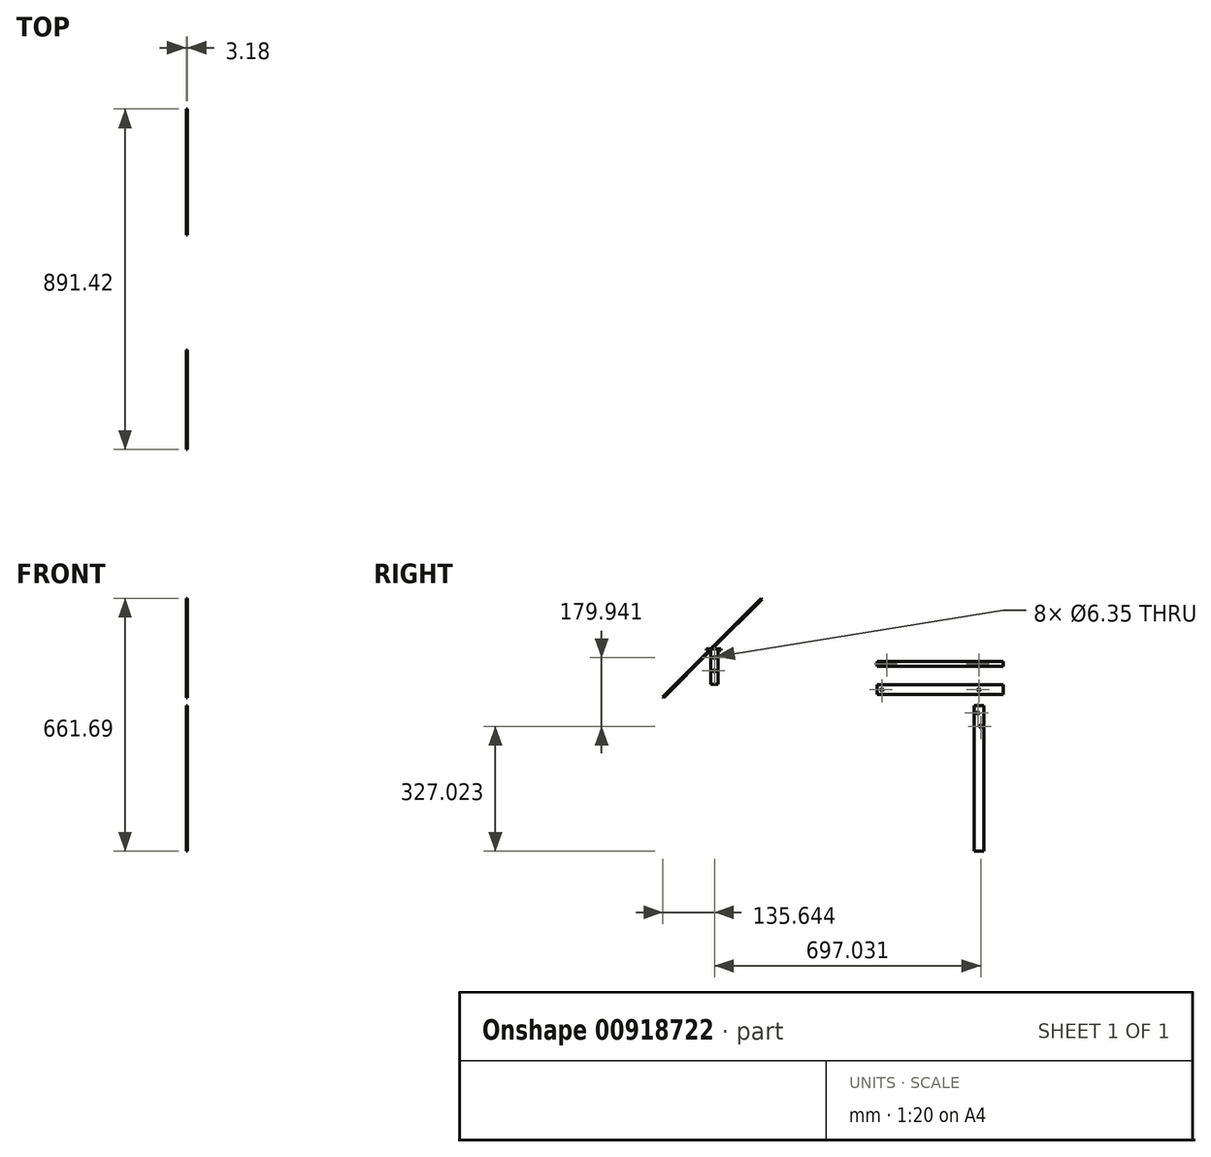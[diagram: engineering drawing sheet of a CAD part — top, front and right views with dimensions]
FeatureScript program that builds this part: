
annotation { "Feature Type Name" : "Feature", "Feature Type Description" : "" }
export const myFeature = defineFeature(function(context is Context, id is Id, definition is map)
    precondition{}
    {
        {
            var Q0;
            Q0=qCreatedBy(makeId("Right.planeOp"),FACE);
            var sketch = newSketch(context, id + "F0", { "sketchPlane" : qUnion([Q0])});
            skLineSegment(sketch, "E0.bottom", {"start": v(29.61, 247) * mm, "end": v(55.01, 247) * mm});
            skLineSegment(sketch, "E0.top", {"start": v(29.61, -134) * mm, "end": v(55.01, -134) * mm});
            skLineSegment(sketch, "E0.left", {"start": v(29.61, 247) * mm, "end": v(29.61, -134) * mm});
            skLineSegment(sketch, "E0.right", {"start": v(55.01, 247) * mm, "end": v(55.01, -134) * mm});
            skCircle(sketch, "E1", {"center": v(39.14, 227.96) * mm, "radius": 3.18 * mm});
            skCircle(sketch, "E2", {"center": v(46.76, 193.03) * mm, "radius": 3.18 * mm});
            skSolve(sketch);
        }
        {
            var Q0;
            Q0 = qSketchRegion(id + "F0", true);
            extrude(context, id + "F1", {"entities" : qUnion([Q0]), "depth" : 3.17 * mm, "offsetDistance" : 25.4 * mm});
        }
        {
            var Q0;
            Q0=qCreatedBy(makeId("Right.planeOp"),FACE);
            var sketch = newSketch(context, id + "F2", { "sketchPlane" : qUnion([Q0])});
            skLineSegment(sketch, "E3.bottom", {"start": v(-224.7, 301.37) * mm, "end": v(105.5, 301.37) * mm});
            skLineSegment(sketch, "E3.top", {"start": v(-224.7, 275.97) * mm, "end": v(105.5, 275.97) * mm});
            skLineSegment(sketch, "E3.left", {"start": v(-224.7, 301.37) * mm, "end": v(-224.7, 275.97) * mm});
            skLineSegment(sketch, "E3.right", {"start": v(105.5, 301.37) * mm, "end": v(105.5, 275.97) * mm});
            skLineSegment(sketch, "E4", {"start": v(105.5, 288.67) * mm, "end": v(-224.7, 288.67) * mm, "construction": true});
            skCircle(sketch, "E5", {"center": v(42, 288.67) * mm, "radius": 3.18 * mm});
            skCircle(sketch, "E6", {"center": v(-212, 288.67) * mm, "radius": 3.18 * mm});
            skLineSegment(sketch, "E7.bottom", {"start": v(105.5, 363.24) * mm, "end": v(-224.7, 363.24) * mm});
            skLineSegment(sketch, "E7.top", {"start": v(105.5, 350.54) * mm, "end": v(-224.7, 350.54) * mm});
            skLineSegment(sketch, "E7.left", {"start": v(105.5, 363.24) * mm, "end": v(105.5, 350.54) * mm});
            skLineSegment(sketch, "E7.right", {"start": v(-224.7, 363.24) * mm, "end": v(-224.7, 350.54) * mm});
            skLineSegment(sketch, "E8", {"start": v(-224.7, 356.9) * mm, "end": v(105.5, 356.9) * mm, "construction": true});
            skCircle(sketch, "E9", {"center": v(42, 356.9) * mm, "radius": 3.18 * mm});
            skCircle(sketch, "E10", {"center": v(-199.3, 356.9) * mm, "radius": 3.18 * mm});
            skLineSegment(sketch, "E11.bottom", {"start": v(-659.8, 392.02) * mm, "end": v(-640.75, 392.02) * mm});
            skLineSegment(sketch, "E11.top", {"start": v(-659.8, 303.12) * mm, "end": v(-640.75, 303.12) * mm});
            skLineSegment(sketch, "E11.left", {"start": v(-659.8, 392.02) * mm, "end": v(-659.8, 303.12) * mm});
            skLineSegment(sketch, "E11.right", {"start": v(-640.75, 392.02) * mm, "end": v(-640.75, 303.12) * mm});
            skLineSegment(sketch, "E12", {"start": v(-650.28, 392.02) * mm, "end": v(-650.28, 303.12) * mm, "construction": true});
            skCircle(sketch, "E13", {"center": v(-650.28, 372.97) * mm, "radius": 3.18 * mm});
            skCircle(sketch, "E14", {"center": v(-650.28, 338.05) * mm, "radius": 3.18 * mm});
            skLineSegment(sketch, "E15.bottom", {"start": v(-656.08, 303.12) * mm, "end": v(-640.75, 303.12) * mm});
            skLineSegment(sketch, "E15.top", {"start": v(-656.08, 302.72) * mm, "end": v(-640.75, 302.72) * mm});
            skLineSegment(sketch, "E15.left", {"start": v(-656.08, 303.12) * mm, "end": v(-656.08, 302.72) * mm});
            skLineSegment(sketch, "E15.right", {"start": v(-640.75, 303.12) * mm, "end": v(-640.75, 302.72) * mm});
            skLineSegment(sketch, "E16.bottom", {"start": v(-671.46, 392.02) * mm, "end": v(-634.1, 392.02) * mm});
            skLineSegment(sketch, "E16.top", {"start": v(-671.46, 395.9) * mm, "end": v(-634.1, 395.9) * mm});
            skLineSegment(sketch, "E16.left", {"start": v(-671.46, 392.02) * mm, "end": v(-671.46, 395.9) * mm});
            skLineSegment(sketch, "E16.right", {"start": v(-634.1, 392.02) * mm, "end": v(-634.1, 395.9) * mm});
            skLineSegment(sketch, "E17", {"start": v(-659.8, 392.02) * mm, "end": v(-783.98, 267.85) * mm});
            skLineSegment(sketch, "E18", {"start": v(-783.98, 267.85) * mm, "end": v(-785.92, 269.78) * mm});
            skLineSegment(sketch, "E19", {"start": v(-785.92, 269.78) * mm, "end": v(-659.8, 395.9) * mm});
            skLineSegment(sketch, "E20", {"start": v(-659.8, 395.9) * mm, "end": v(-659.8, 392.02) * mm});
            skLineSegment(sketch, "E21", {"start": v(-659.8, 392.02) * mm, "end": v(-526.06, 525.76) * mm});
            skLineSegment(sketch, "E22", {"start": v(-526.06, 525.76) * mm, "end": v(-528, 527.7) * mm});
            skLineSegment(sketch, "E23", {"start": v(-659.8, 395.9) * mm, "end": v(-528, 527.7) * mm});
            skSolve(sketch);
        }
        {
            var Q0;
            Q0 = qSketchRegion(id + "F2", true);
            extrude(context, id + "F3", {"entities" : qUnion([Q0]), "depth" : 3.17 * mm, "offsetDistance" : 25.4 * mm});
        }
    });
